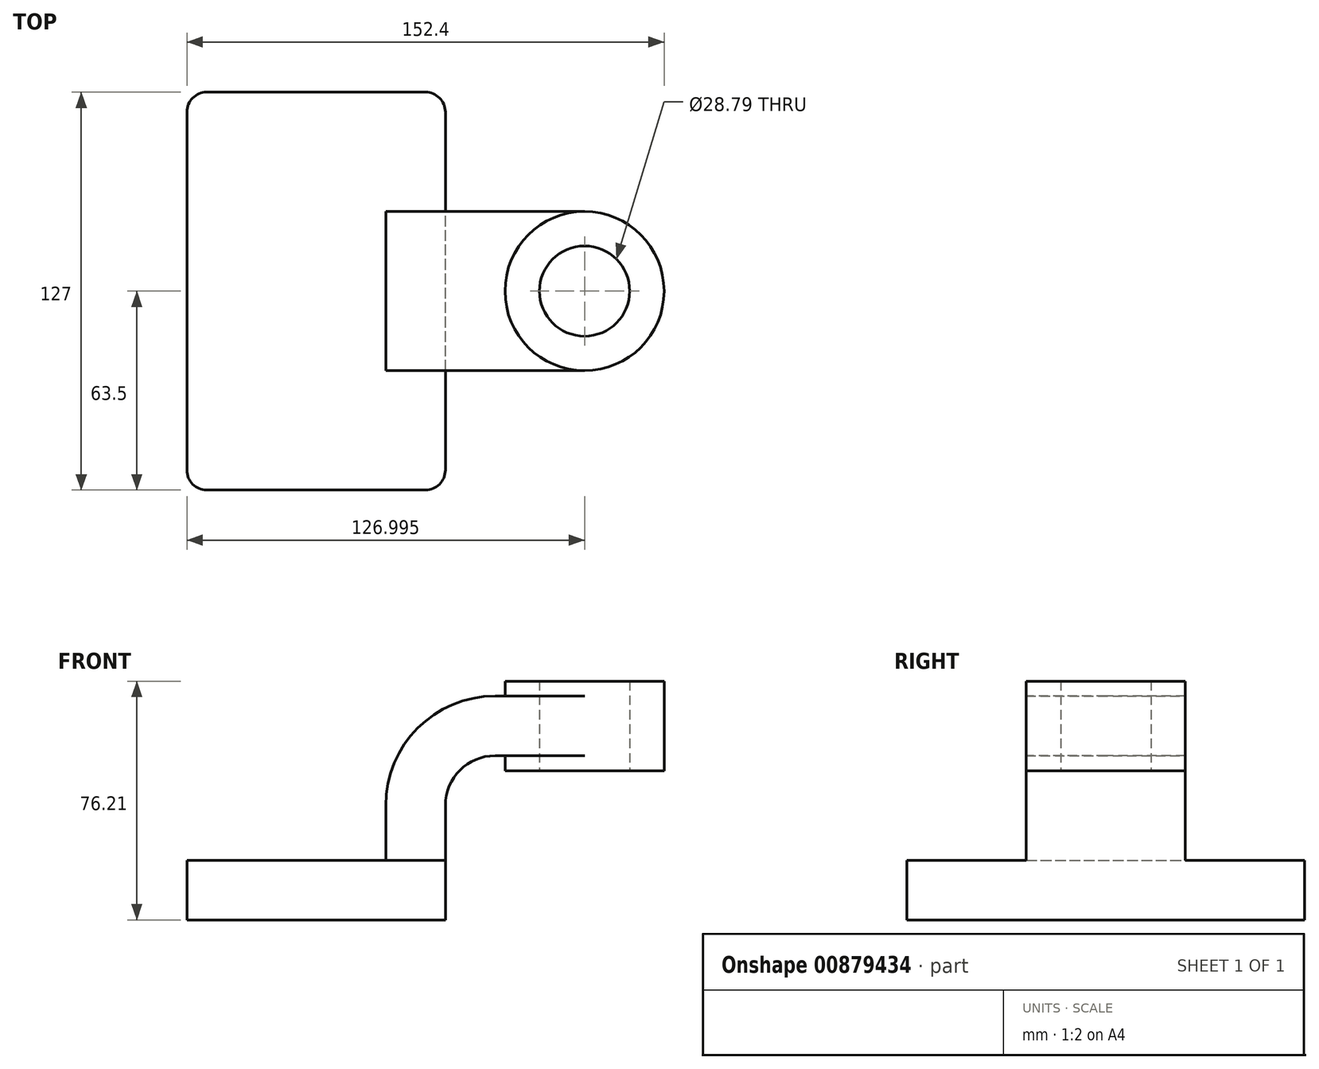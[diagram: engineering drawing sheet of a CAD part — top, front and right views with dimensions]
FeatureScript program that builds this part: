
annotation { "Feature Type Name" : "Feature", "Feature Type Description" : "" }
export const myFeature = defineFeature(function(context is Context, id is Id, definition is map)
    precondition{}
    {
        {
            var Q0;
            Q0=qCreatedBy(makeId("Front.planeOp"),FACE);
            var sketch = newSketch(context, id + "F0", { "sketchPlane" : qUnion([Q0])});
            skLineSegment(sketch, "E0.bottom", {"start": v(-41.28, 9.52) * mm, "end": v(41.28, 9.53) * mm});
            skLineSegment(sketch, "E0.top", {"start": v(-41.28, -9.52) * mm, "end": v(41.28, -9.52) * mm});
            skLineSegment(sketch, "E0.left", {"start": v(-41.28, 9.52) * mm, "end": v(-41.27, -9.53) * mm});
            skLineSegment(sketch, "E0.right", {"start": v(41.28, 9.53) * mm, "end": v(41.28, -9.52) * mm});
            skPoint(sketch, "E0.middle", {"position": v(0, 0) * mm});
            skLineSegment(sketch, "E1.bottom", {"start": v(60.32, 66.68) * mm, "end": v(111.12, 66.68) * mm});
            skLineSegment(sketch, "E1.top", {"start": v(60.32, 38.1) * mm, "end": v(111.12, 38.1) * mm});
            skLineSegment(sketch, "E1.left", {"start": v(60.32, 66.68) * mm, "end": v(60.32, 38.1) * mm});
            skLineSegment(sketch, "E1.right", {"start": v(111.12, 66.68) * mm, "end": v(111.12, 38.1) * mm});
            skPoint(sketch, "E1.middle", {"position": v(85.72, 52.39) * mm});
            skLineSegment(sketch, "E2", {"start": v(41.27, 9.53) * mm, "end": v(41.27, 27) * mm});
            skArc(sketch, "E3", {"start": v(41.27, 27) * mm, "mid": v(45.92, 38.23) * mm, "end": v(57.15, 42.88) * mm});
            skLineSegment(sketch, "E4", {"start": v(57.15, 42.88) * mm, "end": v(85.72, 42.88) * mm});
            skLineSegment(sketch, "E5.0", {"start": v(57.15, 61.93) * mm, "end": v(85.72, 61.93) * mm});
            skArc(sketch, "E5.1", {"start": v(22.22, 27) * mm, "mid": v(32.45, 51.7) * mm, "end": v(57.15, 61.93) * mm});
            skLineSegment(sketch, "E5.2", {"start": v(22.22, 9.53) * mm, "end": v(22.22, 27) * mm});
            skLineSegment(sketch, "E6", {"start": v(85.72, 38.1) * mm, "end": v(85.72, 66.68) * mm});
            skFitSpline(sketch, "E7", {"points": [v(-41.27, 9.53) * mm, v(57.15, 61.93) * mm], "startDerivative": vector(0, 58.64) * mm, "endDerivative": vector(133.86, 0) * mm});
            skLineSegment(sketch, "E8", {"start": v(100.12, 66.68) * mm, "end": v(100.12, 38.1) * mm});
            skSolve(sketch);
        }
        {
            var Q0;
            Q0=makeQuery(id+"F0.imprint","IMPRINT",FACE,{"disambiguationData":[TD([[makeQuery(id+"F0.imprint","IMPRINT",EDGE,{"derivedFrom":sQuery(id+"F0.wireOp",EDGE,"E0.top")}),1.0]])]});
            extrude(context, id + "F1", {"entities" : qUnion([Q0]), "endBound" : BoundingType.SYMMETRIC, "depth" : 127 * mm, "offsetDistance" : 25.4 * mm});
        }
        {
            var Q0;
            {var subQ1=sQuery(id+"F0.wireOp",EDGE,"E2");Q0=makeQuery(id+"F0.imprint","IMPRINT",FACE,{"disambiguationData":[TD([[makeQuery(id+"F0.imprint","IMPRINT",EDGE,{"derivedFrom":subQ1}),1.0]])]});}
            var Q1;
            {var subQ0=sQuery(id+"F0.wireOp",EDGE,"E5.0");var subQ1=sQuery(id+"F0.wireOp",EDGE,"E1.left");var subQ2=makeQuery(id+"F0.imprint","INTERSECT",VERTEX,{"derivedFrom":[subQ1,subQ0]});Q1=makeQuery(id+"F0.imprint","IMPRINT",FACE,{"disambiguationData":[TD([[makeQuery(id+"F0.imprint","IMPRINT",EDGE,{"disambiguationData":[TD([[subQ2,-1.0]])],"derivedFrom":subQ1}),1.0]])]});}
            extrude(context, id + "F2", {"entities" : qUnion([Q0, Q1]), "operationType" : NewBodyOperationType.ADD, "endBound" : BoundingType.SYMMETRIC, "depth" : 50.8 * mm, "offsetDistance" : 25.4 * mm});
        }
        {
            var Q0;
            Q0=makeQuery(id+"F0.imprint","IMPRINT",FACE,{"disambiguationData":[TD([[makeQuery(id+"F0.imprint","IMPRINT",EDGE,{"derivedFrom":sQuery(id+"F0.wireOp",EDGE,"E5.1")}),1.0]])]});
            extrude(context, id + "F3", {"entities" : qUnion([Q0]), "operationType" : NewBodyOperationType.ADD, "endBound" : BoundingType.SYMMETRIC, "depth" : 15.88 * mm, "offsetDistance" : 25.4 * mm});
        }
        {
            var Q0;
            {var subQ0=sQuery(id+"F0.wireOp",EDGE,"E1.right");Q0=makeQuery(id+"F0.imprint","IMPRINT",FACE,{"disambiguationData":[TD([[makeQuery(id+"F0.imprint","IMPRINT",EDGE,{"derivedFrom":subQ0}),-1.0]])]});}
            var Q1;
            Q1=sQuery(id+"F0.wireOp",EDGE,"E6");
            revolve(context, id + "F4", {"operationType" : NewBodyOperationType.ADD, "surfaceOperationType" : NewSurfaceOperationType.NEW, "entities" : qUnion([Q0]), "axis" : qUnion([Q1]), "revolveType" : RevolveType.FULL});
        }
        {
            var Q0;
            Q0=makeQuery(id+"F1.opExtrude","CAP_EDGE",EDGE,{"disambiguationData":[OSD([sQuery(id+"F0.wireOp",EDGE,"E0.left")])],"isStart":false});
            var Q1;
            Q1=makeQuery(id+"F1.opExtrude","CAP_EDGE",EDGE,{"disambiguationData":[OSD([sQuery(id+"F0.wireOp",EDGE,"E0.right")])],"isStart":false});
            var Q2;
            Q2=makeQuery(id+"F1.opExtrude","CAP_EDGE",EDGE,{"disambiguationData":[OSD([sQuery(id+"F0.wireOp",EDGE,"E0.right")])],"isStart":true});
            var Q3;
            Q3=makeQuery(id+"F1.opExtrude","CAP_EDGE",EDGE,{"disambiguationData":[OSD([sQuery(id+"F0.wireOp",EDGE,"E0.left")])],"isStart":true});
            fillet(context, id + "F5", {"entities" : qUnion([Q0, Q1, Q2, Q3]), "radius" : 6.35 * mm, "tangentPropagation" : true, "allowEdgeOverflow" : false});
        }
        {
            var Q0;
            {var subQ5=sQuery(id+"F0.wireOp",EDGE,"E8");Q0=makeQuery(id+"F0.imprint","IMPRINT",FACE,{"disambiguationData":[TD([[makeQuery(id+"F0.imprint","IMPRINT",EDGE,{"derivedFrom":subQ5}),-1.0]])]});}
            var Q1;
            Q1=sQuery(id+"F0.wireOp",EDGE,"E6");
            revolve(context, id + "F6", {"operationType" : NewBodyOperationType.REMOVE, "surfaceOperationType" : NewSurfaceOperationType.NEW, "entities" : qUnion([Q0]), "axis" : qUnion([Q1]), "revolveType" : RevolveType.FULL, "oppositeDirection" : true});
        }
    });
